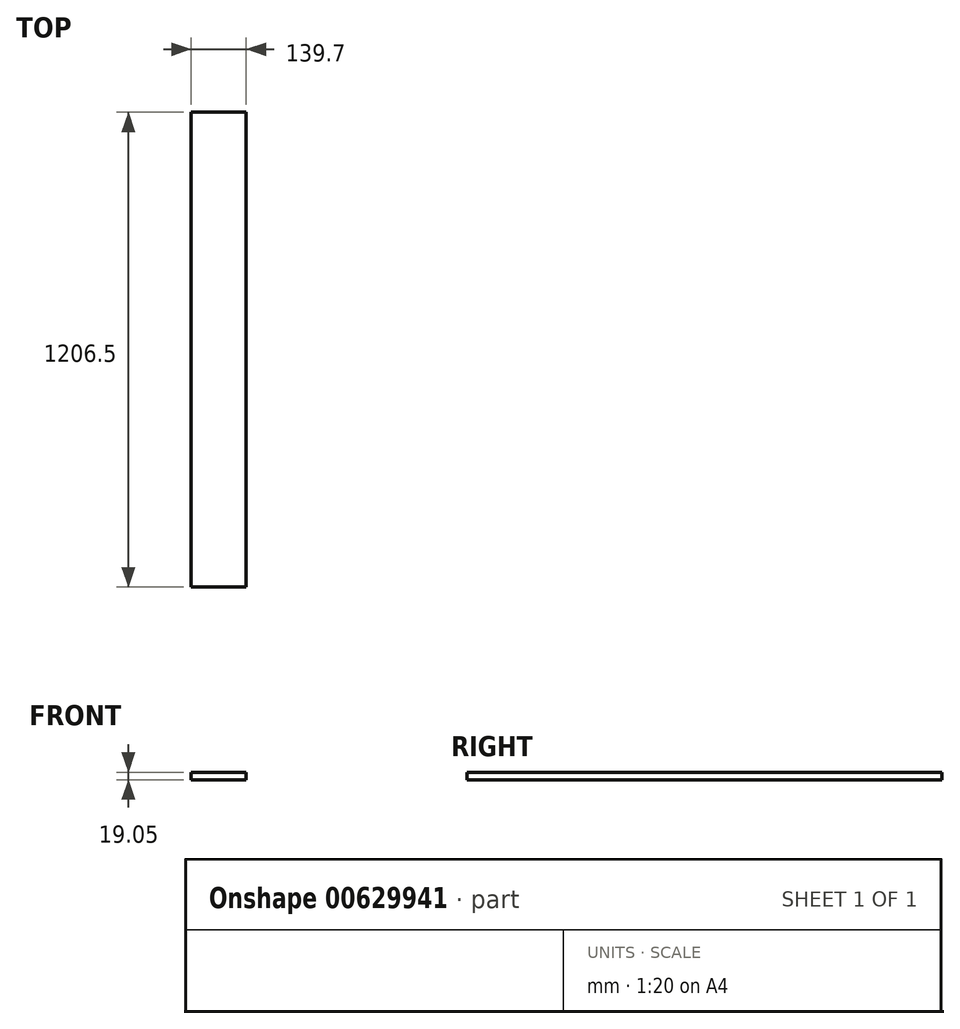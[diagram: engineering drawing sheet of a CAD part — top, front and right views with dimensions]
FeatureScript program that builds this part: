
annotation { "Feature Type Name" : "Feature", "Feature Type Description" : "" }
export const myFeature = defineFeature(function(context is Context, id is Id, definition is map)
    precondition{}
    {
        {
            var Q0;
            Q0=qCreatedBy(makeId("Front.planeOp"),FACE);
            var sketch = newSketch(context, id + "F0", { "sketchPlane" : qUnion([Q0])});
            skLineSegment(sketch, "E0.bottom", {"start": v(-54.29, 21.72) * mm, "end": v(85.41, 21.72) * mm});
            skLineSegment(sketch, "E0.top", {"start": v(-54.29, 2.67) * mm, "end": v(85.41, 2.67) * mm});
            skLineSegment(sketch, "E0.left", {"start": v(-54.29, 21.72) * mm, "end": v(-54.29, 2.67) * mm});
            skLineSegment(sketch, "E0.right", {"start": v(85.41, 21.72) * mm, "end": v(85.41, 2.67) * mm});
            skSolve(sketch);
        }
        {
            var Q0;
            Q0 = qSketchRegion(id + "F0", true);
            extrude(context, id + "F1", {"entities" : qUnion([Q0]), "depth" : 1206.5 * mm, "offsetDistance" : 25.4 * mm});
        }
    });
